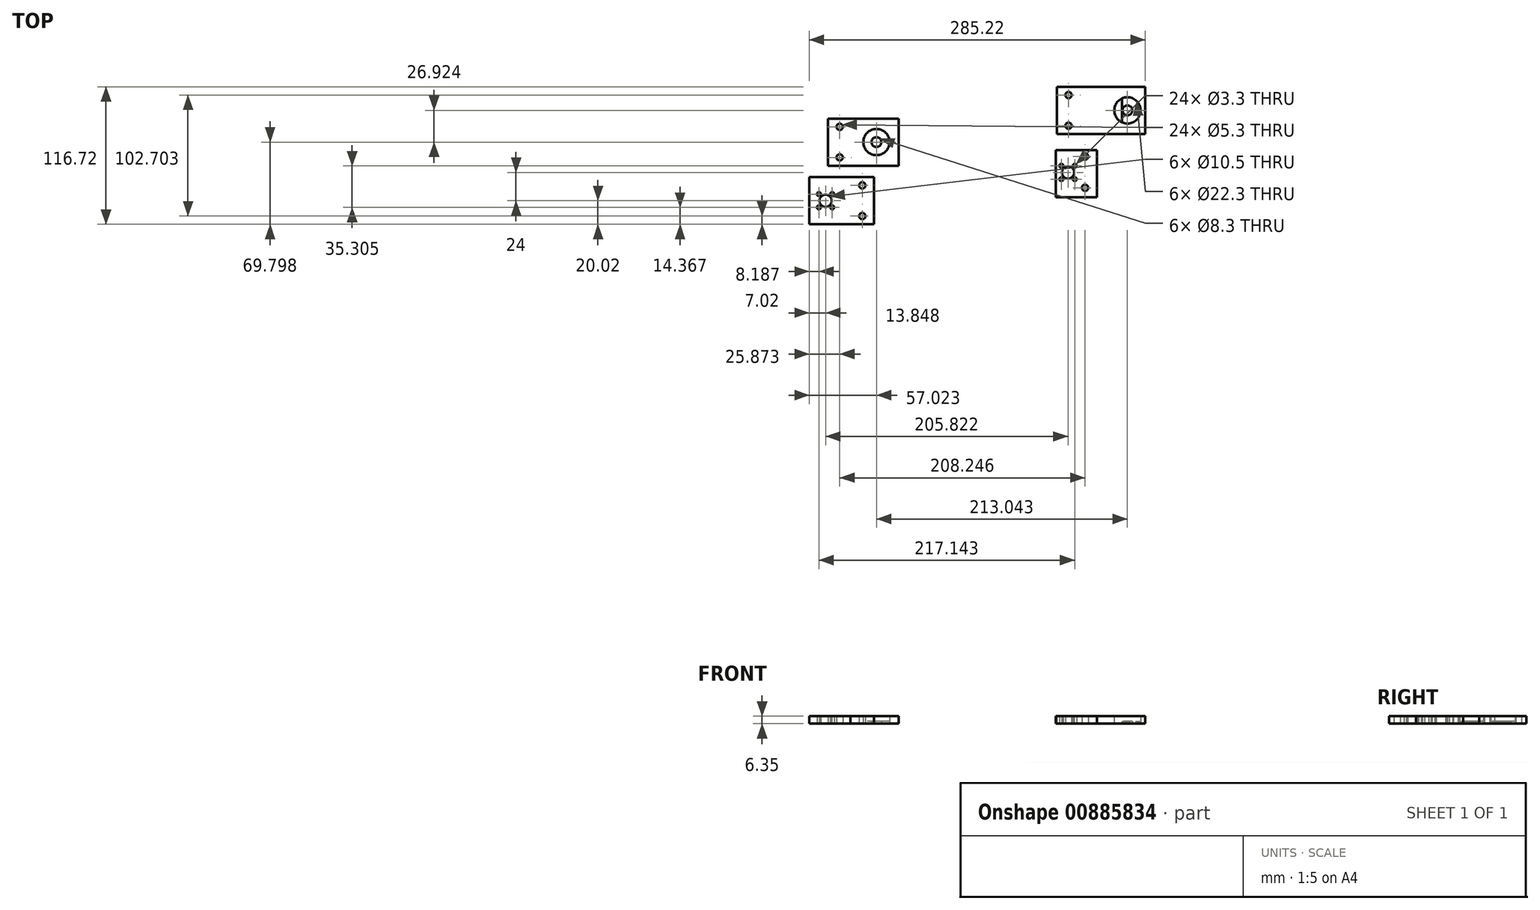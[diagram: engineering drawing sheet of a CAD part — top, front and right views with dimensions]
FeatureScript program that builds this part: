
annotation { "Feature Type Name" : "Feature", "Feature Type Description" : "" }
export const myFeature = defineFeature(function(context is Context, id is Id, definition is map)
    precondition{}
    {
        {
            var Q0;
            Q0=qCreatedBy(makeId("Top.planeOp"),FACE);
            var sketch = newSketch(context, id + "F0", { "sketchPlane" : qUnion([Q0])});
            skLineSegment(sketch, "E0.bottom", {"start": v(-91.93, 42.42) * mm, "end": v(-71.93, 42.42) * mm});
            skLineSegment(sketch, "E0.top", {"start": v(-91.93, 2.42) * mm, "end": v(-71.93, 2.42) * mm});
            skLineSegment(sketch, "E0.left", {"start": v(-91.93, 42.42) * mm, "end": v(-91.93, 2.42) * mm});
            skLineSegment(sketch, "E0.right", {"start": v(-71.93, 42.42) * mm, "end": v(-71.93, 2.42) * mm});
            skCircle(sketch, "E1", {"center": v(-81.93, 35.42) * mm, "radius": 2.65 * mm});
            skCircle(sketch, "E2", {"center": v(-81.93, 9.42) * mm, "radius": 2.65 * mm});
            skPoint(sketch, "E3", {"position": v(-71.93, 42.42) * mm});
            skPoint(sketch, "E4", {"position": v(-71.93, 2.42) * mm});
            skLineSegment(sketch, "E5.bottom", {"start": v(-71.93, 42.42) * mm, "end": v(-31.93, 42.42) * mm});
            skLineSegment(sketch, "E5.top", {"start": v(-71.93, 2.42) * mm, "end": v(-31.93, 2.42) * mm});
            skLineSegment(sketch, "E5.right", {"start": v(-31.93, 42.42) * mm, "end": v(-31.93, 2.42) * mm});
            skCircle(sketch, "E6", {"center": v(-50.78, 22.42) * mm, "radius": 4.15 * mm});
            skCircle(sketch, "E7", {"center": v(-50.78, 22.42) * mm, "radius": 11.15 * mm});
            skLineSegment(sketch, "E8.bottom", {"start": v(102.27, 69.34) * mm, "end": v(122.27, 69.34) * mm});
            skLineSegment(sketch, "E8.top", {"start": v(102.27, 29.34) * mm, "end": v(122.27, 29.34) * mm});
            skLineSegment(sketch, "E8.left", {"start": v(102.27, 69.34) * mm, "end": v(102.27, 29.34) * mm});
            skLineSegment(sketch, "E8.right", {"start": v(122.27, 69.34) * mm, "end": v(122.27, 29.34) * mm});
            skCircle(sketch, "E9", {"center": v(112.27, 62.34) * mm, "radius": 2.65 * mm});
            skCircle(sketch, "E10", {"center": v(112.27, 36.34) * mm, "radius": 2.65 * mm});
            skPoint(sketch, "E11", {"position": v(122.27, 69.34) * mm});
            skPoint(sketch, "E12", {"position": v(122.27, 29.34) * mm});
            skLineSegment(sketch, "E13.bottom", {"start": v(122.27, 69.34) * mm, "end": v(157.6, 69.34) * mm});
            skLineSegment(sketch, "E13.top", {"start": v(122.27, 29.34) * mm, "end": v(157.6, 29.34) * mm});
            skLineSegment(sketch, "E13.right", {"start": v(157.6, 69.34) * mm, "end": v(157.6, 29.34) * mm});
            skCircle(sketch, "E14", {"center": v(162.27, 49.34) * mm, "radius": 4.15 * mm});
            skCircle(sketch, "E15", {"center": v(162.27, 49.34) * mm, "radius": 11.15 * mm});
            skLineSegment(sketch, "E16.bottom", {"start": v(157.6, 69.34) * mm, "end": v(177.42, 69.34) * mm});
            skLineSegment(sketch, "E16.top", {"start": v(157.6, 29.34) * mm, "end": v(177.42, 29.34) * mm});
            skLineSegment(sketch, "E16.right", {"start": v(177.42, 69.34) * mm, "end": v(177.42, 29.34) * mm});
            skSolve(sketch);
        }
        {
            var Q0;
            Q0=qCreatedBy(makeId("Top.planeOp"),FACE);
            var sketch = newSketch(context, id + "F1", { "sketchPlane" : qUnion([Q0])});
            skLineSegment(sketch, "E17.bottom", {"start": v(-52.8, -47.36) * mm, "end": v(-72.8, -47.36) * mm});
            skLineSegment(sketch, "E17.top", {"start": v(-52.8, -7.36) * mm, "end": v(-72.8, -7.36) * mm});
            skLineSegment(sketch, "E17.left", {"start": v(-52.8, -47.36) * mm, "end": v(-52.8, -7.36) * mm});
            skLineSegment(sketch, "E17.right", {"start": v(-72.8, -47.36) * mm, "end": v(-72.8, -7.36) * mm});
            skCircle(sketch, "E18", {"center": v(-62.8, -40.36) * mm, "radius": 2.65 * mm});
            skCircle(sketch, "E19", {"center": v(-62.8, -14.36) * mm, "radius": 2.65 * mm});
            skLineSegment(sketch, "E20.bottom", {"start": v(-72.8, -7.36) * mm, "end": v(-102.8, -7.36) * mm});
            skLineSegment(sketch, "E20.top", {"start": v(-72.8, -47.38) * mm, "end": v(-102.9, -47.38) * mm});
            skLineSegment(sketch, "E20.left", {"start": v(-72.8, -7.36) * mm, "end": v(-72.8, -47.38) * mm});
            skCircle(sketch, "E21", {"center": v(-93.95, -27.36) * mm, "radius": 5.25 * mm});
            skLineSegment(sketch, "E22.bottom", {"start": v(-102.8, -7.36) * mm, "end": v(-107.8, -7.36) * mm});
            skLineSegment(sketch, "E22.top", {"start": v(-102.9, -47.38) * mm, "end": v(-107.8, -47.38) * mm});
            skLineSegment(sketch, "E22.right", {"start": v(-107.8, -7.36) * mm, "end": v(-107.8, -47.38) * mm});
            skCircle(sketch, "E23", {"center": v(-99.61, -21.7) * mm, "radius": 1.65 * mm});
            skCircle(sketch, "E24", {"center": v(-88.3, -21.7) * mm, "radius": 1.65 * mm});
            skCircle(sketch, "E25", {"center": v(-88.3, -33.01) * mm, "radius": 1.65 * mm});
            skCircle(sketch, "E26", {"center": v(-99.61, -33.01) * mm, "radius": 1.65 * mm});
            skLineSegment(sketch, "E27.right", {"start": v(-104.07, -17.43) * mm, "end": v(-104.07, -37.43) * mm});
            skLineSegment(sketch, "E28.left", {"start": v(136.32, -24.27) * mm, "end": v(136.32, 15.73) * mm});
            skCircle(sketch, "E29", {"center": v(126.32, -16.36) * mm, "radius": 2.65 * mm});
            skCircle(sketch, "E30", {"center": v(126.32, 10.16) * mm, "radius": 2.65 * mm});
            skCircle(sketch, "E31", {"center": v(111.87, -3.36) * mm, "radius": 5.25 * mm});
            skCircle(sketch, "E32", {"center": v(106.2, 2.3) * mm, "radius": 1.65 * mm});
            skCircle(sketch, "E33", {"center": v(117.53, 2.3) * mm, "radius": 1.65 * mm});
            skCircle(sketch, "E34", {"center": v(117.53, -9.01) * mm, "radius": 1.65 * mm});
            skCircle(sketch, "E35", {"center": v(106.2, -9.01) * mm, "radius": 1.65 * mm});
            skLineSegment(sketch, "E36.bottom", {"start": v(136.32, 15.73) * mm, "end": v(101.52, 15.73) * mm});
            skLineSegment(sketch, "E36.top", {"start": v(136.32, -24.27) * mm, "end": v(101.52, -24.27) * mm});
            skLineSegment(sketch, "E36.left", {"start": v(136.32, 15.73) * mm, "end": v(136.32, -24.27) * mm});
            skLineSegment(sketch, "E36.right", {"start": v(101.52, 15.73) * mm, "end": v(101.52, -24.27) * mm});
            skLineSegment(sketch, "E37", {"start": v(-99.61, -33.01) * mm, "end": v(-88.3, -21.7) * mm, "construction": true});
            skLineSegment(sketch, "E38", {"start": v(-99.61, -21.7) * mm, "end": v(-88.3, -33.01) * mm, "construction": true});
            skLineSegment(sketch, "E39", {"start": v(106.2, 2.3) * mm, "end": v(117.53, -9.01) * mm, "construction": true});
            skLineSegment(sketch, "E40", {"start": v(117.53, 2.3) * mm, "end": v(106.2, -9.01) * mm, "construction": true});
            skLineSegment(sketch, "E41", {"start": v(116.32, 15.73) * mm, "end": v(116.32, -24.27) * mm});
            skCircle(sketch, "E42", {"center": v(111.87, -3.36) * mm, "radius": 4 * mm, "construction": true});
            skSolve(sketch);
        }
        {
            var Q0;
            {var subQ4=sQuery(id+"F1.wireOp",EDGE,"E20.bottom");Q0=makeQuery(id+"F1.imprint","IMPRINT",FACE,{"disambiguationData":[TD([[makeQuery(id+"F1.imprint","IMPRINT",EDGE,{"derivedFrom":subQ4}),1.0]])]});}
            var Q1;
            {var subQ1=sQuery(id+"F1.wireOp",EDGE,"E17.bottom");Q1=makeQuery(id+"F1.imprint","IMPRINT",FACE,{"disambiguationData":[TD([[makeQuery(id+"F1.imprint","IMPRINT",EDGE,{"derivedFrom":subQ1}),-1.0]])]});}
            var Q2;
            {var subQ0=sQuery(id+"F1.wireOp",EDGE,"d900b7f6-d9c4-4d91-b376-dae8aba15a70.bottom");Q2=makeQuery(id+"F1.imprint","IMPRINT",FACE,{"disambiguationData":[TD([[makeQuery(id+"F1.imprint","IMPRINT",EDGE,{"derivedFrom":subQ0}),1.0]])]});}
            var Q3;
            {var subQ1=sQuery(id+"F1.wireOp",EDGE,"E28.bottom");Q3=makeQuery(id+"F1.imprint","IMPRINT",FACE,{"disambiguationData":[TD([[makeQuery(id+"F1.imprint","IMPRINT",EDGE,{"derivedFrom":subQ1}),-1.0]])]});}
            var Q4;
            Q4=makeQuery(id+"F1.imprint","IMPRINT",FACE,{"disambiguationData":[TD([[makeQuery(id+"F1.imprint","IMPRINT",EDGE,{"derivedFrom":sQuery(id+"F1.wireOp",EDGE,"E31")}),-1.0]])]});
            var Q5;
            Q5=makeQuery(id+"F1.imprint","IMPRINT",FACE,{"disambiguationData":[TD([[makeQuery(id+"F1.imprint","IMPRINT",EDGE,{"derivedFrom":sQuery(id+"F1.wireOp",EDGE,"E29")}),-1.0]])]});
            extrude(context, id + "F2", {"entities" : qUnion([Q0, Q1, Q2, Q3, Q4, Q5]), "offsetDistance" : 25 * mm, "depth" : 6.35 * mm});
        }
        {
            var Q0;
            Q0=qSketchRegion(id+"F0",true);
            var Q1;
            Q1=makeQuery(id+"F0.imprint","IMPRINT",FACE,{"disambiguationData":[TD([[makeQuery(id+"F0.imprint","IMPRINT",EDGE,{"derivedFrom":sQuery(id+"F0.wireOp",EDGE,"a7c15d13-0d06-4db3-b24c-167334b71ffd")}),1.0]])]});
            extrude(context, id + "F3", {"entities" : qUnion([Q0, Q1]), "depth" : 6.35 * mm, "offsetDistance" : 25 * mm});
        }
        {
            var Q0;
            Q0=makeQuery(id+"F0.imprint","IMPRINT",FACE,{"disambiguationData":[TD([[makeQuery(id+"F0.imprint","IMPRINT",EDGE,{"derivedFrom":sQuery(id+"F0.wireOp",EDGE,"E6")}),-1.0]])]});
            var Q1;
            {var subQ0=sQuery(id+"F0.wireOp",EDGE,"E13.right");var subQ1=sQuery(id+"F0.wireOp",EDGE,"E15");var subQ2=makeQuery(id+"F0.imprint","INTERSECT",VERTEX,{"disambiguationData":[OD(0.0)],"derivedFrom":[subQ1,subQ0]});Q1=makeQuery(id+"F0.imprint","IMPRINT",FACE,{"disambiguationData":[TD([[makeQuery(id+"F0.imprint","IMPRINT",EDGE,{"disambiguationData":[TD([[subQ2,-1.0]])],"derivedFrom":subQ1}),1.0]])]});}
            var Q2;
            Q2=makeQuery(id+"F0.imprint","IMPRINT",FACE,{"disambiguationData":[TD([[makeQuery(id+"F0.imprint","IMPRINT",EDGE,{"derivedFrom":sQuery(id+"F0.wireOp",EDGE,"E14")}),-1.0]])]});
            extrude(context, id + "F4", {"entities" : qUnion([Q0, Q1, Q2]), "depth" : 2 * mm, "offsetDistance" : 25 * mm});
        }
    });
